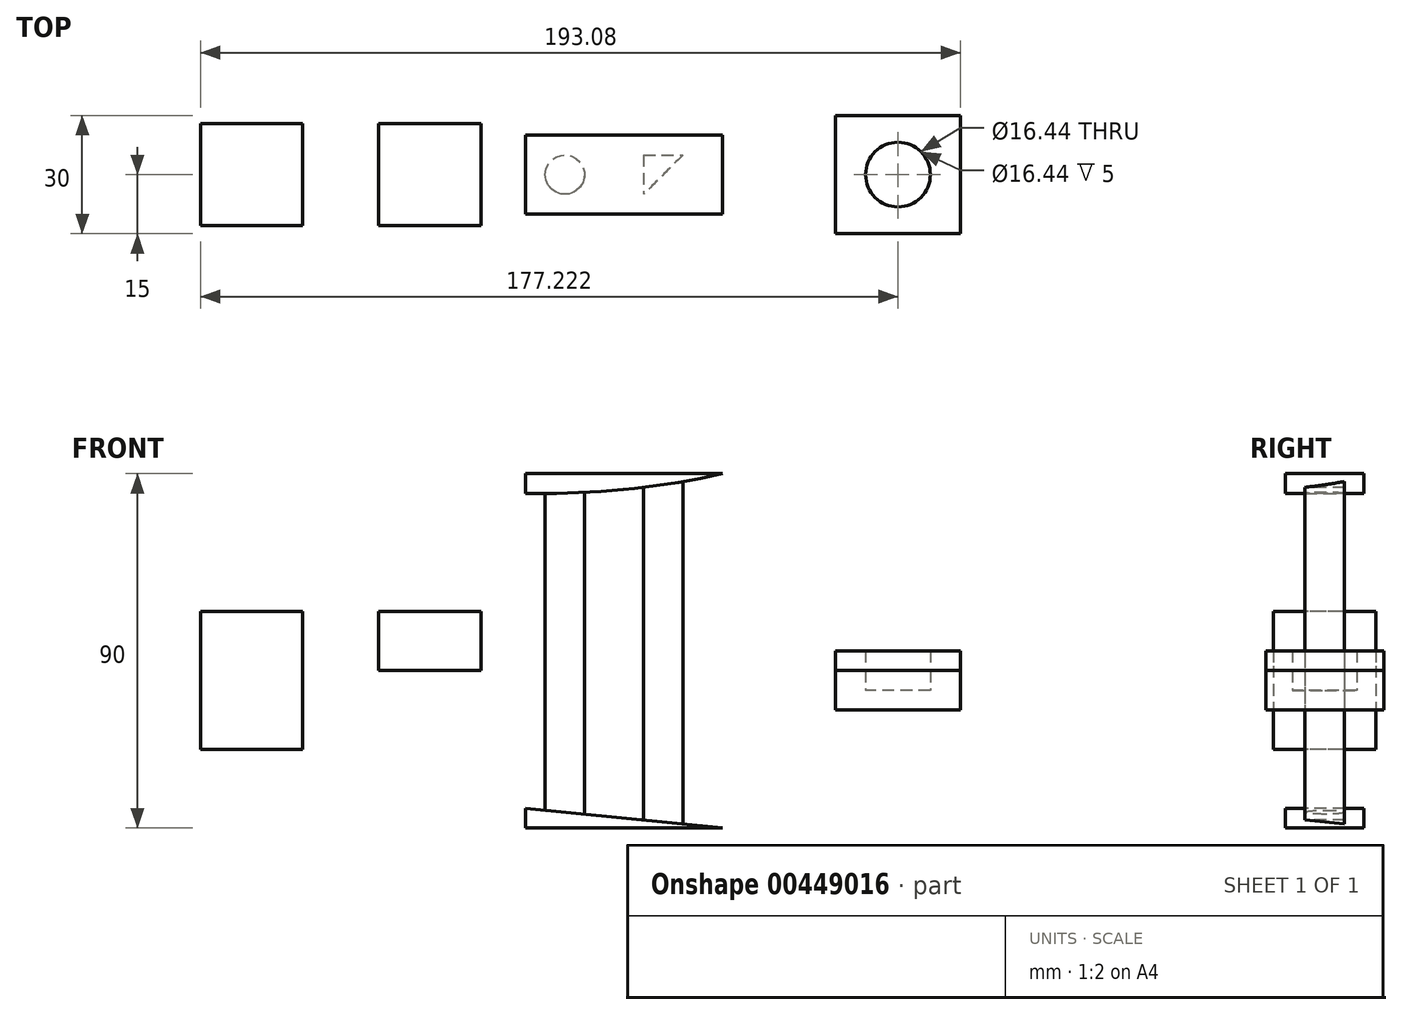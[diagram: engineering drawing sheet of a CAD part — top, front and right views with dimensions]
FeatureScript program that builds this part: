
annotation { "Feature Type Name" : "Feature", "Feature Type Description" : "" }
export const myFeature = defineFeature(function(context is Context, id is Id, definition is map)
    precondition{}
    {
        {
            var Q0;
            Q0=qCreatedBy(makeId("Top.planeOp"),FACE);
            var sketch = newSketch(context, id + "F0", { "sketchPlane" : qUnion([Q0])});
            skLineSegment(sketch, "E0.bottom", {"start": v(-13, 13) * mm, "end": v(13, 13) * mm});
            skLineSegment(sketch, "E0.top", {"start": v(-13, -13) * mm, "end": v(13, -13) * mm});
            skLineSegment(sketch, "E0.left", {"start": v(-13, 13) * mm, "end": v(-13, -13) * mm});
            skLineSegment(sketch, "E0.right", {"start": v(13, 13) * mm, "end": v(13, -13) * mm});
            skPoint(sketch, "E0.middle", {"position": v(0, 0) * mm});
            skSolve(sketch);
        }
        {
            var Q0;
            Q0=qCreatedBy(makeId("Top.planeOp"),FACE);
            var sketch = newSketch(context, id + "F1", { "sketchPlane" : qUnion([Q0])});
            skLineSegment(sketch, "E1.bottom", {"start": v(32.23, 13) * mm, "end": v(58.23, 13) * mm});
            skLineSegment(sketch, "E1.top", {"start": v(32.23, -13) * mm, "end": v(58.23, -13) * mm});
            skLineSegment(sketch, "E1.left", {"start": v(32.23, 13) * mm, "end": v(32.23, -13) * mm});
            skLineSegment(sketch, "E1.right", {"start": v(58.23, 13) * mm, "end": v(58.23, -13) * mm});
            skPoint(sketch, "E1.middle", {"position": v(45.23, 0) * mm});
            skSolve(sketch);
        }
        {
            var Q0;
            Q0=qCreatedBy(makeId("Front.planeOp"),FACE);
            var sketch = newSketch(context, id + "F2", { "sketchPlane" : qUnion([Q0])});
            skLineSegment(sketch, "E2.bottom", {"start": v(69.59, 0) * mm, "end": v(119.59, 0) * mm});
            skLineSegment(sketch, "E2.top", {"start": v(69.59, 5) * mm, "end": v(119.59, 5) * mm});
            skLineSegment(sketch, "E2.left", {"start": v(69.59, 0) * mm, "end": v(69.59, 5) * mm});
            skLineSegment(sketch, "E2.right", {"start": v(119.59, 0) * mm, "end": v(119.59, 5) * mm});
            skLineSegment(sketch, "E3.bottom", {"start": v(69.59, 5) * mm, "end": v(74.59, 5) * mm});
            skLineSegment(sketch, "E3.top", {"start": v(69.59, 55) * mm, "end": v(74.59, 55) * mm});
            skLineSegment(sketch, "E3.left", {"start": v(69.59, 5) * mm, "end": v(69.59, 55) * mm});
            skLineSegment(sketch, "E3.right", {"start": v(74.59, 5) * mm, "end": v(74.59, 55) * mm});
            skLineSegment(sketch, "E4.bottom", {"start": v(69.59, 55) * mm, "end": v(119.59, 55) * mm});
            skLineSegment(sketch, "E4.top", {"start": v(69.59, 60) * mm, "end": v(119.59, 60) * mm});
            skLineSegment(sketch, "E4.left", {"start": v(69.59, 55) * mm, "end": v(69.59, 60) * mm});
            skLineSegment(sketch, "E4.right", {"start": v(119.59, 55) * mm, "end": v(119.59, 60) * mm});
            skLineSegment(sketch, "E5.MirrorCS", {"start": v(69.59, -5) * mm, "end": v(119.59, -5) * mm});
            skLineSegment(sketch, "E6", {"start": v(69.59, -5) * mm, "end": v(69.59, 0) * mm});
            skLineSegment(sketch, "E7", {"start": v(119.59, -5) * mm, "end": v(119.59, 0) * mm});
            skArc(sketch, "E8", {"start": v(74.59, 55) * mm, "mid": v(97.22, 56.25) * mm, "end": v(119.59, 60) * mm});
            skLineSegment(sketch, "E9.bottom", {"start": v(119.59, -25) * mm, "end": v(69.59, -25) * mm});
            skLineSegment(sketch, "E9.top", {"start": v(119.59, -30) * mm, "end": v(69.59, -30) * mm});
            skLineSegment(sketch, "E9.left", {"start": v(119.59, -25) * mm, "end": v(119.59, -30) * mm});
            skLineSegment(sketch, "E9.right", {"start": v(69.59, -25) * mm, "end": v(69.59, -30) * mm});
            skLineSegment(sketch, "E10", {"start": v(69.59, -25) * mm, "end": v(119.59, -30) * mm});
            skSolve(sketch);
        }
        {
            var Q0;
            Q0=makeQuery(id+"F2.imprint","IMPRINT",FACE,{"disambiguationData":[TD([[makeQuery(id+"F2.imprint","IMPRINT",EDGE,{"derivedFrom":sQuery(id+"F2.wireOp",EDGE,"E4.top")}),-1.0]])]});
            var Q1;
            {var subQ0=sQuery(id+"F2.wireOp",EDGE,"d88ff40e-2887-472f-8713-1230f44090761.MirrorCS");Q1=makeQuery(id+"F2.imprint","IMPRINT",FACE,{"disambiguationData":[TD([[makeQuery(id+"F2.imprint","IMPRINT",EDGE,{"derivedFrom":subQ0}),1.0]])]});}
            var Q2;
            Q2=makeQuery(id+"F2.imprint","IMPRINT",FACE,{"disambiguationData":[TD([[makeQuery(id+"F2.imprint","IMPRINT",EDGE,{"derivedFrom":sQuery(id+"F2.wireOp",EDGE,"E9.top")}),-1.0]])]});
            extrude(context, id + "F3", {"entities" : qUnion([Q0, Q1, Q2]), "endBound" : BoundingType.SYMMETRIC, "oppositeDirection" : true, "depth" : 20 * mm});
        }
        {
            var Q0;
            Q0=qCreatedBy(makeId("Top.planeOp"),FACE);
            var sketch = newSketch(context, id + "F4", { "sketchPlane" : qUnion([Q0])});
            skLineSegment(sketch, "E11.0.0", {"start": v(69.59, -10) * mm, "end": v(119.59, -10) * mm, "construction": true});
            skLineSegment(sketch, "E11.0.1", {"start": v(119.59, -10) * mm, "end": v(119.59, 10) * mm, "construction": true});
            skLineSegment(sketch, "E11.0.2", {"start": v(119.59, 10) * mm, "end": v(69.59, 10) * mm, "construction": true});
            skLineSegment(sketch, "E11.0.3", {"start": v(69.59, 10) * mm, "end": v(69.59, -10) * mm, "construction": true});
            skLineSegment(sketch, "E12.bottom", {"start": v(109.59, -5) * mm, "end": v(99.59, -5) * mm});
            skLineSegment(sketch, "E12.top", {"start": v(109.59, 5) * mm, "end": v(99.59, 5) * mm});
            skLineSegment(sketch, "E12.left", {"start": v(109.59, -5) * mm, "end": v(109.59, 5) * mm});
            skLineSegment(sketch, "E12.right", {"start": v(99.59, -5) * mm, "end": v(99.59, 5) * mm});
            skLineSegment(sketch, "E13", {"start": v(99.59, -5) * mm, "end": v(109.59, 5) * mm});
            skCircle(sketch, "E14", {"center": v(79.59, 0) * mm, "radius": 5 * mm});
            skLineSegment(sketch, "E15", {"start": v(119.59, 0) * mm, "end": v(69.59, 0) * mm, "construction": true});
            skPoint(sketch, "E16", {"position": v(104.59, 0) * mm});
            skSolve(sketch);
        }
        {
            var Q0;
            Q0=qCreatedBy(makeId("Top.planeOp"),FACE);
            var sketch = newSketch(context, id + "F5", { "sketchPlane" : qUnion([Q0])});
            skLineSegment(sketch, "E17.bottom", {"start": v(148.37, 15) * mm, "end": v(180.08, 15) * mm});
            skLineSegment(sketch, "E17.top", {"start": v(148.37, -15) * mm, "end": v(180.08, -15) * mm});
            skLineSegment(sketch, "E17.left", {"start": v(148.37, 15) * mm, "end": v(148.37, -15) * mm});
            skLineSegment(sketch, "E17.right", {"start": v(180.08, 15) * mm, "end": v(180.08, -15) * mm});
            skPoint(sketch, "E17.middle", {"position": v(164.22, 0) * mm});
            skSolve(sketch);
        }
        {
            var Q0;
            Q0=makeQuery(id+"F5.imprint","IMPRINT",FACE,{"disambiguationData":[TD([[makeQuery(id+"F5.imprint","IMPRINT",EDGE,{"derivedFrom":sQuery(id+"F5.wireOp",EDGE,"E17.bottom")}),-1.0]])]});
            extrude(context, id + "F6", {"entities" : qUnion([Q0]), "depth" : 10 * mm});
        }
        {
            var Q0;
            Q0=makeQuery(id+"F6.opExtrude","CAP_FACE",FACE,{"disambiguationData":[OSD([sQuery(id+"F5.wireOp",EDGE,"E17.bottom"),sQuery(id+"F5.wireOp",EDGE,"E17.top"),sQuery(id+"F5.wireOp",EDGE,"E17.left"),sQuery(id+"F5.wireOp",EDGE,"E17.right")])],"isStart":false});
            var sketch = newSketch(context, id + "F7", { "sketchPlane" : qUnion([Q0])});
            skCircle(sketch, "E18", {"center": v(164.22, 0) * mm, "radius": 8.22 * mm});
            skPoint(sketch, "E18.centerSnap0", {"position": v(164.22, 15) * mm});
            skPoint(sketch, "E18.centerSnap1", {"position": v(148.37, 0) * mm});
            skSolve(sketch);
        }
        {
            var Q0;
            Q0=makeQuery(id+"F6.opExtrude","CAP_FACE",FACE,{"disambiguationData":[OSD([sQuery(id+"F5.wireOp",EDGE,"E17.bottom"),sQuery(id+"F5.wireOp",EDGE,"E17.top"),sQuery(id+"F5.wireOp",EDGE,"E17.left"),sQuery(id+"F5.wireOp",EDGE,"E17.right")])],"isStart":false});
            extrude(context, id + "F8", {"entities" : qUnion([Q0]), "depth" : 5 * mm});
        }
        {
            var Q0;
            Q0=makeQuery(id+"F0.imprint","IMPRINT",FACE,{"disambiguationData":[TD([[makeQuery(id+"F0.imprint","IMPRINT",EDGE,{"derivedFrom":sQuery(id+"F0.wireOp",EDGE,"E0.bottom")}),-1.0]])]});
            extrude(context, id + "F9", {"entities" : qUnion([Q0]), "depth" : 25 * mm, "hasSecondDirection" : true, "secondDirectionOppositeDirection" : true, "secondDirectionDepth" : 10 * mm});
        }
        {
            var Q0;
            Q0=makeQuery(id+"F1.imprint","IMPRINT",FACE,{"disambiguationData":[TD([[makeQuery(id+"F1.imprint","IMPRINT",EDGE,{"derivedFrom":sQuery(id+"F1.wireOp",EDGE,"E1.bottom")}),-1.0]])]});
            extrude(context, id + "F10", {"entities" : qUnion([Q0]), "depth" : 25 * mm, "hasSecondDirection" : true, "secondDirectionOppositeDirection" : false, "secondDirectionDepth" : 10 * mm});
        }
        {
            var Q0;
            Q0=makeQuery(id+"F4.imprint","IMPRINT",FACE,{"disambiguationData":[TD([[makeQuery(id+"F4.imprint","IMPRINT",EDGE,{"derivedFrom":sQuery(id+"F4.wireOp",EDGE,"E14")}),1.0]])]});
            var Q1;
            Q1=makeQuery(id+"F4.imprint","IMPRINT",FACE,{"disambiguationData":[TD([[makeQuery(id+"F4.imprint","IMPRINT",EDGE,{"derivedFrom":sQuery(id+"F4.wireOp",EDGE,"E12.top")}),1.0]])]});
            var Q2;
            Q2=makeQuery(id+"F3.opExtrude","SWEPT_FACE",FACE,{"disambiguationData":[OSD([sQuery(id+"F2.wireOp",EDGE,"E8")])]});
            var Q3;
            Q3=makeQuery(id+"F3.opExtrude","SWEPT_BODY",BODY,{"disambiguationData":[OSD([sQuery(id+"F2.wireOp",EDGE,"E4.bottom"),sQuery(id+"F2.wireOp",EDGE,"E4.top"),sQuery(id+"F2.wireOp",EDGE,"E4.left"),sQuery(id+"F2.wireOp",EDGE,"E8")])]});
            var Q4;
            Q4=makeQuery(id+"F3.opExtrude","SWEPT_FACE",FACE,{"disambiguationData":[OSD([sQuery(id+"F2.wireOp",EDGE,"E10")])]});
            extrude(context, id + "F11", {"entities" : qUnion([Q0, Q1]), "endBound" : BoundingType.UP_TO_NEXT, "endBoundEntityFace" : qUnion([Q2]), "endBoundEntityBody" : qUnion([Q3]), "depth" : 25 * mm, "hasSecondDirection" : true, "secondDirectionBound" : SecondDirectionBoundingType.UP_TO_SURFACE, "secondDirectionOppositeDirection" : true, "secondDirectionBoundEntityFace" : qUnion([Q4]), "secondDirectionDepth" : 25 * mm});
        }
        {
            var Q0;
            Q0=makeQuery(id+"F7.imprint","IMPRINT",FACE,{"disambiguationData":[TD([[makeQuery(id+"F7.imprint","IMPRINT",EDGE,{"derivedFrom":sQuery(id+"F7.wireOp",EDGE,"E18")}),1.0]])]});
            extrude(context, id + "F12", {"entities" : qUnion([Q0]), "operationType" : NewBodyOperationType.REMOVE, "endBound" : BoundingType.THROUGH_ALL, "depth" : 25 * mm, "hasSecondDirection" : true, "secondDirectionOppositeDirection" : true, "secondDirectionDepth" : 5 * mm});
        }
    });
